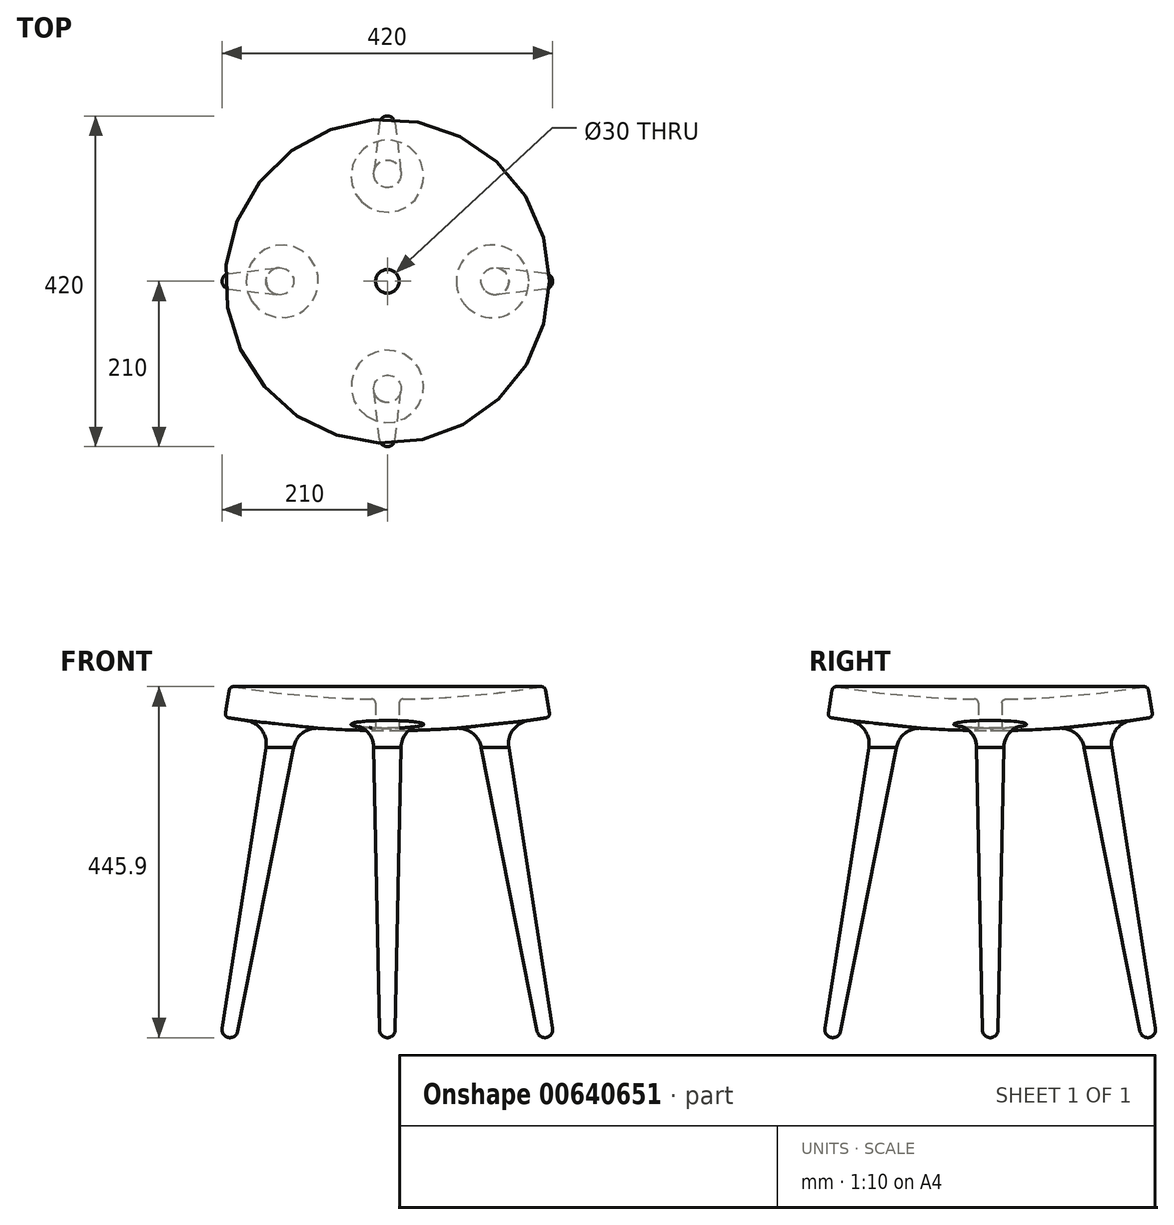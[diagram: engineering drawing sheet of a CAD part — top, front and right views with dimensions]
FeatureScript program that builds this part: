
annotation { "Feature Type Name" : "Feature", "Feature Type Description" : "" }
export const myFeature = defineFeature(function(context is Context, id is Id, definition is map)
    precondition{}
    {
        {
            var Q0;
            Q0=qCreatedBy(makeId("Front.planeOp"),FACE);
            var sketch = newSketch(context, id + "F0", { "sketchPlane" : qUnion([Q0])});
            skArc(sketch, "E0", {"start": v(0, 390) * mm, "mid": v(103.66, 394.3) * mm, "end": v(206.61, 407.2) * mm});
            skLineSegment(sketch, "E1", {"start": v(0, 1640) * mm, "end": v(0, 0) * mm, "construction": true});
            skLineSegment(sketch, "E2", {"start": v(200, 446.64) * mm, "end": v(206.61, 407.2) * mm});
            skArc(sketch, "E3.0", {"start": v(0, 430) * mm, "mid": v(100.35, 434.17) * mm, "end": v(200, 446.64) * mm});
            skLineSegment(sketch, "E4", {"start": v(0, 430) * mm, "end": v(0, 390) * mm});
            skSolve(sketch);
        }
        {
            var Q0;
            Q0=makeQuery(id+"F0.imprint","IMPRINT",FACE,{"disambiguationData":[TD([[makeQuery(id+"F0.imprint","IMPRINT",EDGE,{"derivedFrom":sQuery(id+"F0.wireOp",EDGE,"E0")}),1.0]])]});
            var Q1;
            Q1=sQuery(id+"F0.wireOp",EDGE,"E1");
            revolve(context, id + "F1", {"entities" : qUnion([Q0]), "axis" : qUnion([Q1]), "revolveType" : RevolveType.FULL});
        }
        {
            var Q0;
            Q0=qCreatedBy(makeId("Front.planeOp"),FACE);
            var sketch = newSketch(context, id + "F2", { "sketchPlane" : qUnion([Q0])});
            skLineSegment(sketch, "E5", {"start": v(0, 0) * mm, "end": v(-270.55, 0) * mm, "construction": true});
            skArc(sketch, "E6", {"start": v(-201.74, 0.15) * mm, "mid": v(-194.35, 1.75) * mm, "end": v(-190.19, 8.07) * mm});
            skLineSegment(sketch, "E7", {"start": v(-201.74, 0.15) * mm, "end": v(-130.54, 403.92) * mm});
            skLineSegment(sketch, "E8", {"start": v(-130.54, 403.92) * mm, "end": v(-112.88, 400.44) * mm});
            skLineSegment(sketch, "E9", {"start": v(-112.88, 400.44) * mm, "end": v(-190.19, 8.07) * mm});
            skSolve(sketch);
        }
        {
            var Q0;
            Q0 = qSketchRegion(id + "F2", true);
            var Q1;
            Q1=sQuery(id+"F2.wireOp",EDGE,"E7");
            revolve(context, id + "F3", {"entities" : qUnion([Q0]), "axis" : qUnion([Q1]), "revolveType" : RevolveType.FULL});
        }
        {
            var Q0;
            Q0=qCreatedBy(makeId("Front.planeOp"),FACE);
            var sketch = newSketch(context, id + "F4", { "sketchPlane" : qUnion([Q0])});
            skLineSegment(sketch, "E10", {"start": v(0, 0) * mm, "end": v(0, 104.44) * mm, "construction": true});
            skSolve(sketch);
        }
        {
            var Q0;
            Q0=makeQuery(id+"F3.opRevolve","SWEPT_BODY",BODY,{"disambiguationData":[OSD([sQuery(id+"F2.wireOp",EDGE,"E6"),sQuery(id+"F2.wireOp",EDGE,"E7"),sQuery(id+"F2.wireOp",EDGE,"E8"),sQuery(id+"F2.wireOp",EDGE,"E9")])]});
            var Q1;
            Q1=sQuery(id+"F4.wireOp",EDGE,"E10");
            circularPattern(context, id + "F5", {"entities" : qUnion([Q0]), "axis" : qUnion([Q1]), "angle" : 360 * degree, "instanceCount" : 4, "equalSpace" : true});
        }
        {
            var Q0;
            Q0=makeQuery(id+"F3.opRevolve","SWEPT_BODY",BODY,{"disambiguationData":[OSD([sQuery(id+"F2.wireOp",EDGE,"E6"),sQuery(id+"F2.wireOp",EDGE,"E7"),sQuery(id+"F2.wireOp",EDGE,"E8"),sQuery(id+"F2.wireOp",EDGE,"E9")])]});
            var Q1;
            Q1=makeQuery(id+"F5.opPattern","COPY",BODY,{"derivedFrom":makeQuery(id+"F3.opRevolve","SWEPT_BODY",BODY,{"disambiguationData":[OSD([sQuery(id+"F2.wireOp",EDGE,"E6"),sQuery(id+"F2.wireOp",EDGE,"E7"),sQuery(id+"F2.wireOp",EDGE,"E8"),sQuery(id+"F2.wireOp",EDGE,"E9")])]}),"instanceName":"3"});
            var Q2;
            Q2=makeQuery(id+"F1.opRevolve","SWEPT_BODY",BODY,{"disambiguationData":[OSD([sQuery(id+"F0.wireOp",EDGE,"E0"),sQuery(id+"F0.wireOp",EDGE,"E2"),sQuery(id+"F0.wireOp",EDGE,"E3.0"),sQuery(id+"F0.wireOp",EDGE,"E4")])]});
            var Q3;
            Q3=makeQuery(id+"F5.opPattern","COPY",BODY,{"derivedFrom":makeQuery(id+"F3.opRevolve","SWEPT_BODY",BODY,{"disambiguationData":[OSD([sQuery(id+"F2.wireOp",EDGE,"E6"),sQuery(id+"F2.wireOp",EDGE,"E7"),sQuery(id+"F2.wireOp",EDGE,"E8"),sQuery(id+"F2.wireOp",EDGE,"E9")])]}),"instanceName":"2"});
            var Q4;
            Q4=makeQuery(id+"F5.opPattern","COPY",BODY,{"derivedFrom":makeQuery(id+"F3.opRevolve","SWEPT_BODY",BODY,{"disambiguationData":[OSD([sQuery(id+"F2.wireOp",EDGE,"E6"),sQuery(id+"F2.wireOp",EDGE,"E7"),sQuery(id+"F2.wireOp",EDGE,"E8"),sQuery(id+"F2.wireOp",EDGE,"E9")])]}),"instanceName":"1"});
            booleanBodies(context, id + "F6", {"operationType" : BooleanOperationType.UNION, "tools" : qUnion([Q0, Q1, Q2, Q3, Q4])});
        }
        {
            var Q0;
            Q0=makeQuery(id+"F6.opBoolean","INTERSECT",EDGE,{"derivedFrom":[makeQuery(id+"F1.opRevolve","SWEPT_FACE",FACE,{"disambiguationData":[OSD([sQuery(id+"F0.wireOp",EDGE,"E0")])]}),makeQuery(id+"F5.opPattern","COPY",FACE,{"derivedFrom":makeQuery(id+"F3.opRevolve","SWEPT_FACE",FACE,{"disambiguationData":[OSD([sQuery(id+"F2.wireOp",EDGE,"E9")])]}),"instanceName":"1"})]});
            var Q1;
            Q1=makeQuery(id+"F6.opBoolean","INTERSECT",EDGE,{"derivedFrom":[makeQuery(id+"F1.opRevolve","SWEPT_FACE",FACE,{"disambiguationData":[OSD([sQuery(id+"F0.wireOp",EDGE,"E0")])]}),makeQuery(id+"F3.opRevolve","SWEPT_FACE",FACE,{"disambiguationData":[OSD([sQuery(id+"F2.wireOp",EDGE,"E9")])]})]});
            var Q2;
            Q2=makeQuery(id+"F6.opBoolean","INTERSECT",EDGE,{"derivedFrom":[makeQuery(id+"F1.opRevolve","SWEPT_FACE",FACE,{"disambiguationData":[OSD([sQuery(id+"F0.wireOp",EDGE,"E0")])]}),makeQuery(id+"F5.opPattern","COPY",FACE,{"derivedFrom":makeQuery(id+"F3.opRevolve","SWEPT_FACE",FACE,{"disambiguationData":[OSD([sQuery(id+"F2.wireOp",EDGE,"E9")])]}),"instanceName":"3"})]});
            var Q3;
            Q3=makeQuery(id+"F6.opBoolean","INTERSECT",EDGE,{"derivedFrom":[makeQuery(id+"F1.opRevolve","SWEPT_FACE",FACE,{"disambiguationData":[OSD([sQuery(id+"F0.wireOp",EDGE,"E0")])]}),makeQuery(id+"F5.opPattern","COPY",FACE,{"derivedFrom":makeQuery(id+"F3.opRevolve","SWEPT_FACE",FACE,{"disambiguationData":[OSD([sQuery(id+"F2.wireOp",EDGE,"E9")])]}),"instanceName":"2"})]});
            fillet(context, id + "F7", {"entities" : qUnion([Q0, Q1, Q2, Q3]), "radius" : 30 * mm, "tangentPropagation" : true, "allowEdgeOverflow" : false});
        }
        {
            var Q0;
            Q0=makeQuery(id+"F1.opRevolve","SWEPT_EDGE",EDGE,{"disambiguationData":[OSD([sQuery(id+"F0.wireOp",EDGE,"E2"),sQuery(id+"F0.wireOp",EDGE,"E3.0")])]});
            var Q1;
            Q1=makeQuery(id+"F1.opRevolve","SWEPT_EDGE",EDGE,{"disambiguationData":[OSD([sQuery(id+"F0.wireOp",EDGE,"E0"),sQuery(id+"F0.wireOp",EDGE,"E2")])]});
            fillet(context, id + "F8", {"entities" : qUnion([Q0, Q1]), "radius" : 5 * mm, "tangentPropagation" : true, "allowEdgeOverflow" : false});
        }
        {
            var Q0;
            Q0=qCreatedBy(makeId("Top.planeOp"),FACE);
            var sketch = newSketch(context, id + "F9", { "sketchPlane" : qUnion([Q0])});
            skCircle(sketch, "E11", {"center": v(0, 0) * mm, "radius": 15 * mm});
            skSolve(sketch);
        }
        {
            var Q0;
            Q0 = qSketchRegion(id + "F9", true);
            extrude(context, id + "F10", {"entities" : qUnion([Q0]), "operationType" : NewBodyOperationType.REMOVE, "endBound" : BoundingType.THROUGH_ALL, "depth" : 25 * mm, "offsetDistance" : 25 * mm});
        }
        {
            var Q0;
            Q0=makeQuery(id+"F10.boolean.opBoolean","INTERSECT",EDGE,{"derivedFrom":[makeQuery(id+"F1.opRevolve","SWEPT_FACE",FACE,{"disambiguationData":[OSD([sQuery(id+"F0.wireOp",EDGE,"E3.0")])]}),makeQuery(id+"F10.opExtrude","SWEPT_FACE",FACE,{"disambiguationData":[OSD([sQuery(id+"F9.wireOp",EDGE,"E11")])]})]});
            var Q1;
            Q1=makeQuery(id+"F10.boolean.opBoolean","INTERSECT",EDGE,{"derivedFrom":[makeQuery(id+"F1.opRevolve","SWEPT_FACE",FACE,{"disambiguationData":[OSD([sQuery(id+"F0.wireOp",EDGE,"E0")])]}),makeQuery(id+"F10.opExtrude","SWEPT_FACE",FACE,{"disambiguationData":[OSD([sQuery(id+"F9.wireOp",EDGE,"E11")])]})]});
            fillet(context, id + "F11", {"entities" : qUnion([Q0, Q1]), "radius" : 5 * mm, "tangentPropagation" : true, "allowEdgeOverflow" : false});
        }
    });
